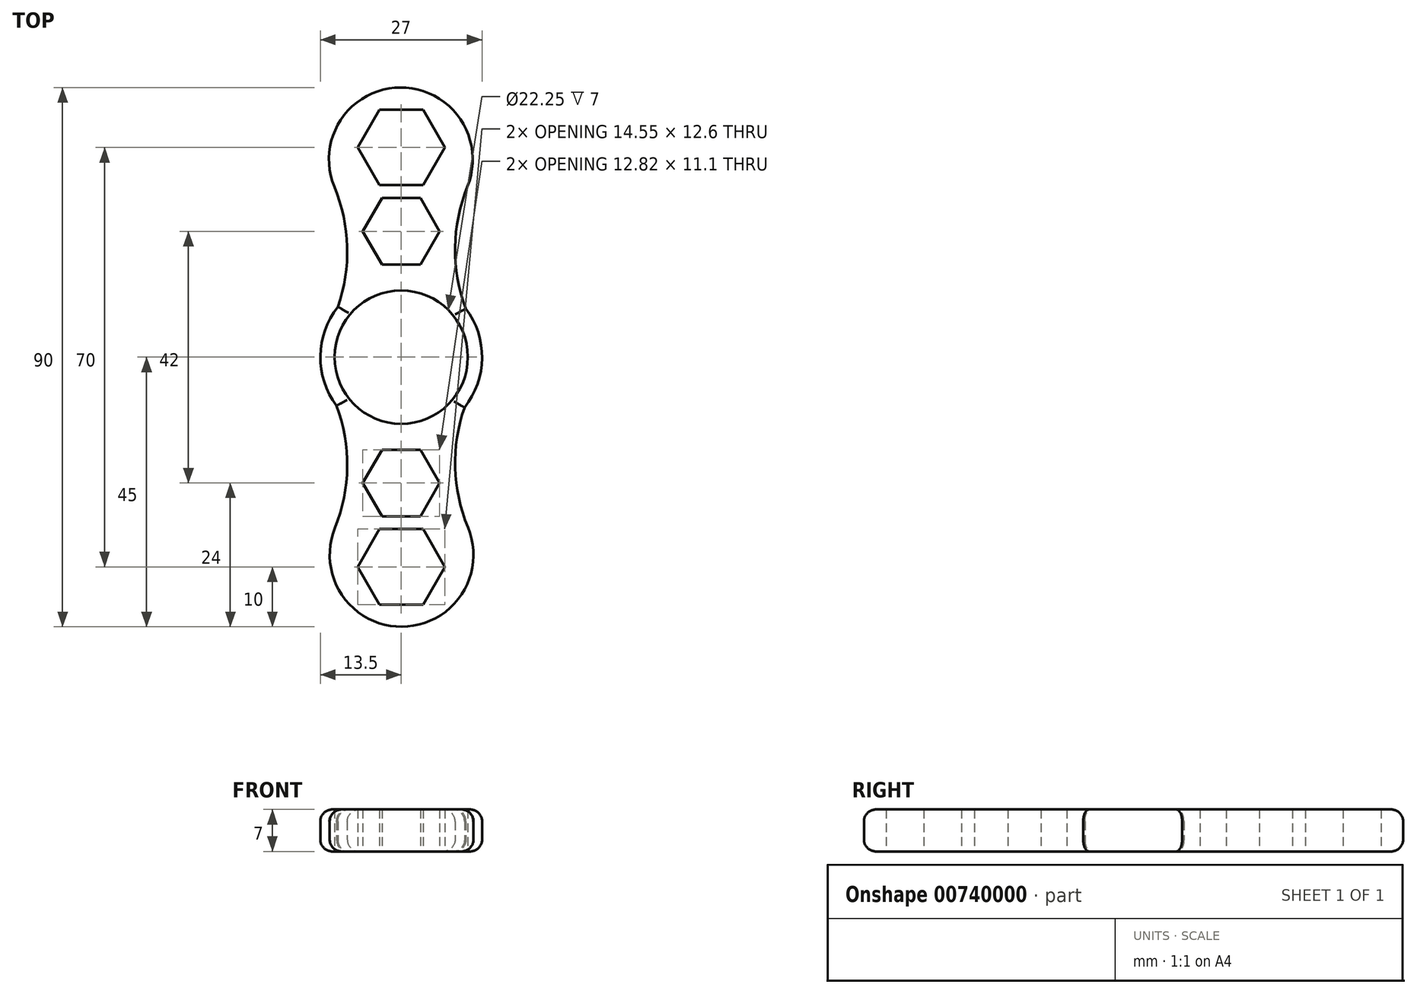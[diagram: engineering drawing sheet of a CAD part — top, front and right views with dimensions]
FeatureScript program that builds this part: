
annotation { "Feature Type Name" : "Feature", "Feature Type Description" : "" }
export const myFeature = defineFeature(function(context is Context, id is Id, definition is map)
    precondition{}
    {
        {
            var Q0;
            Q0=qCreatedBy(makeId("Top.planeOp"),FACE);
            var sketch = newSketch(context, id + "F0", { "sketchPlane" : qUnion([Q0])});
            skCircle(sketch, "E0", {"center": v(0, 0) * mm, "radius": 11.12 * mm});
            skCircle(sketch, "E1.cCircle", {"center": v(0, 21) * mm, "radius": 5.55 * mm, "construction": true});
            skLineSegment(sketch, "E1.0", {"start": v(3.2, 15.45) * mm, "end": v(-3.2, 15.45) * mm});
            skLineSegment(sketch, "E1.1", {"start": v(-3.2, 15.45) * mm, "end": v(-6.4, 21) * mm});
            skLineSegment(sketch, "E1.2", {"start": v(-6.4, 21) * mm, "end": v(-3.2, 26.55) * mm});
            skLineSegment(sketch, "E1.3", {"start": v(-3.2, 26.55) * mm, "end": v(3.2, 26.55) * mm});
            skLineSegment(sketch, "E1.4", {"start": v(3.2, 26.55) * mm, "end": v(6.4, 21) * mm});
            skLineSegment(sketch, "E1.5", {"start": v(6.4, 21) * mm, "end": v(3.2, 15.45) * mm});
            skPoint(sketch, "E1.0.midPoint", {"position": v(0, 15.45) * mm});
            skArc(sketch, "E2", {"start": v(-13.18, 2.92) * mm, "mid": v(0.28, -13.5) * mm, "end": v(13.05, 3.46) * mm});
            skArc(sketch, "E3", {"start": v(-5.62, 22.36) * mm, "mid": v(-5.51, 22.3) * mm, "end": v(-5.4, 22.25) * mm});
            skArc(sketch, "E4", {"start": v(-13.18, 2.92) * mm, "mid": v(-9.09, 15.41) * mm, "end": v(-11.15, 28.4) * mm});
            skArc(sketch, "E5", {"start": v(11.05, 28.49) * mm, "mid": v(9.09, 15.74) * mm, "end": v(13.05, 3.46) * mm});
            skPoint(sketch, "E6", {"position": v(0, 26.55) * mm});
            skCircle(sketch, "E7.cCircle", {"center": v(0, 35) * mm, "radius": 6.3 * mm, "construction": true});
            skLineSegment(sketch, "E7.0", {"start": v(3.64, 28.7) * mm, "end": v(-3.64, 28.7) * mm});
            skLineSegment(sketch, "E7.1", {"start": v(-3.64, 28.7) * mm, "end": v(-7.27, 35) * mm});
            skLineSegment(sketch, "E7.2", {"start": v(-7.27, 35) * mm, "end": v(-3.64, 41.3) * mm});
            skLineSegment(sketch, "E7.3", {"start": v(-3.64, 41.3) * mm, "end": v(3.64, 41.3) * mm});
            skLineSegment(sketch, "E7.4", {"start": v(3.64, 41.3) * mm, "end": v(7.27, 35) * mm});
            skLineSegment(sketch, "E7.5", {"start": v(7.27, 35) * mm, "end": v(3.64, 28.7) * mm});
            skPoint(sketch, "E7.0.midPoint", {"position": v(0, 28.7) * mm});
            skArc(sketch, "E8.trimOffspring", {"start": v(5.4, 22.31) * mm, "mid": v(5.5, 22.37) * mm, "end": v(5.6, 22.42) * mm});
            skArc(sketch, "E9.trimOffspring", {"start": v(11.05, 28.49) * mm, "mid": v(-0.12, 45) * mm, "end": v(-11.15, 28.4) * mm});
            skSolve(sketch);
        }
        {
            var Q0;
            Q0=makeQuery(id+"F0.imprint","IMPRINT",FACE,{"disambiguationData":[TD([[makeQuery(id+"F0.imprint","IMPRINT",EDGE,{"derivedFrom":sQuery(id+"F0.wireOp",EDGE,"E0")}),-1.0]])]});
            extrude(context, id + "F1", {"entities" : qUnion([Q0]), "depth" : 7 * mm, "offsetDistance" : 25 * mm});
        }
        {
            var Q0;
            Q0=makeQuery(id+"F1.opExtrude","SWEPT_BODY",BODY,{"disambiguationData":[OSD([sQuery(id+"F0.wireOp",EDGE,"E0"),sQuery(id+"F0.wireOp",EDGE,"E1.0"),sQuery(id+"F0.wireOp",EDGE,"E1.1"),sQuery(id+"F0.wireOp",EDGE,"E1.2"),sQuery(id+"F0.wireOp",EDGE,"E1.3"),sQuery(id+"F0.wireOp",EDGE,"E1.4"),sQuery(id+"F0.wireOp",EDGE,"E1.5"),sQuery(id+"F0.wireOp",EDGE,"E2"),sQuery(id+"F0.wireOp",EDGE,"E4"),sQuery(id+"F0.wireOp",EDGE,"E5"),sQuery(id+"F0.wireOp",EDGE,"E7.0"),sQuery(id+"F0.wireOp",EDGE,"E7.1"),sQuery(id+"F0.wireOp",EDGE,"E7.2"),sQuery(id+"F0.wireOp",EDGE,"E7.3"),sQuery(id+"F0.wireOp",EDGE,"E7.4"),sQuery(id+"F0.wireOp",EDGE,"E7.5"),sQuery(id+"F0.wireOp",EDGE,"E9.trimOffspring")])]});
            var Q1;
            Q1=makeQuery(id+"F1.opExtrude","CAP_EDGE",EDGE,{"disambiguationData":[OSD([sQuery(id+"F0.wireOp",EDGE,"E0")])],"isStart":false});
            circularPattern(context, id + "F2", {"entities" : qUnion([Q0]), "axis" : qUnion([Q1]), "angle" : 360 * degree, "instanceCount" : 2, "equalSpace" : true});
        }
        {
            var Q0;
            Q0=makeQuery(id+"F2.opPattern","COPY",BODY,{"derivedFrom":makeQuery(id+"F1.opExtrude","SWEPT_BODY",BODY,{"disambiguationData":[OSD([sQuery(id+"F0.wireOp",EDGE,"E0"),sQuery(id+"F0.wireOp",EDGE,"E1.0"),sQuery(id+"F0.wireOp",EDGE,"E1.1"),sQuery(id+"F0.wireOp",EDGE,"E1.2"),sQuery(id+"F0.wireOp",EDGE,"E1.3"),sQuery(id+"F0.wireOp",EDGE,"E1.4"),sQuery(id+"F0.wireOp",EDGE,"E1.5"),sQuery(id+"F0.wireOp",EDGE,"E2"),sQuery(id+"F0.wireOp",EDGE,"E4"),sQuery(id+"F0.wireOp",EDGE,"E5"),sQuery(id+"F0.wireOp",EDGE,"E7.0"),sQuery(id+"F0.wireOp",EDGE,"E7.1"),sQuery(id+"F0.wireOp",EDGE,"E7.2"),sQuery(id+"F0.wireOp",EDGE,"E7.3"),sQuery(id+"F0.wireOp",EDGE,"E7.4"),sQuery(id+"F0.wireOp",EDGE,"E7.5"),sQuery(id+"F0.wireOp",EDGE,"E9.trimOffspring")])]}),"instanceName":"1"});
            var Q1;
            Q1=makeQuery(id+"F1.opExtrude","SWEPT_BODY",BODY,{"disambiguationData":[OSD([sQuery(id+"F0.wireOp",EDGE,"E0"),sQuery(id+"F0.wireOp",EDGE,"E1.0"),sQuery(id+"F0.wireOp",EDGE,"E1.1"),sQuery(id+"F0.wireOp",EDGE,"E1.2"),sQuery(id+"F0.wireOp",EDGE,"E1.3"),sQuery(id+"F0.wireOp",EDGE,"E1.4"),sQuery(id+"F0.wireOp",EDGE,"E1.5"),sQuery(id+"F0.wireOp",EDGE,"E2"),sQuery(id+"F0.wireOp",EDGE,"E4"),sQuery(id+"F0.wireOp",EDGE,"E5"),sQuery(id+"F0.wireOp",EDGE,"E7.0"),sQuery(id+"F0.wireOp",EDGE,"E7.1"),sQuery(id+"F0.wireOp",EDGE,"E7.2"),sQuery(id+"F0.wireOp",EDGE,"E7.3"),sQuery(id+"F0.wireOp",EDGE,"E7.4"),sQuery(id+"F0.wireOp",EDGE,"E7.5"),sQuery(id+"F0.wireOp",EDGE,"E9.trimOffspring")])]});
            booleanBodies(context, id + "F3", {"operationType" : BooleanOperationType.UNION, "tools" : qUnion([Q0, Q1])});
        }
        {
            var Q0;
            Q0=makeQuery(id+"F1.opExtrude","CAP_EDGE",EDGE,{"disambiguationData":[OSD([sQuery(id+"F0.wireOp",EDGE,"E9.trimOffspring")])],"isStart":false});
            var Q1;
            Q1=makeQuery(id+"F1.opExtrude","CAP_EDGE",EDGE,{"disambiguationData":[OSD([sQuery(id+"F0.wireOp",EDGE,"E4")])],"isStart":false});
            var Q2;
            {var subQ0=makeQuery(id+"F1.opExtrude","CAP_EDGE",EDGE,{"disambiguationData":[OSD([sQuery(id+"F0.wireOp",EDGE,"E2")])],"isStart":false});Q2=makeQuery(id+"F3.opBoolean","MERGE",EDGE,{"disambiguationData":[OD(0.0)],"derivedFrom":[subQ0,makeQuery(id+"F2.opPattern","COPY",EDGE,{"derivedFrom":subQ0,"instanceName":"1"})]});}
            var Q3;
            Q3=makeQuery(id+"F2.opPattern","COPY",EDGE,{"derivedFrom":makeQuery(id+"F1.opExtrude","CAP_EDGE",EDGE,{"disambiguationData":[OSD([sQuery(id+"F0.wireOp",EDGE,"E5")])],"isStart":false}),"instanceName":"1"});
            var Q4;
            Q4=makeQuery(id+"F2.opPattern","COPY",EDGE,{"derivedFrom":makeQuery(id+"F1.opExtrude","CAP_EDGE",EDGE,{"disambiguationData":[OSD([sQuery(id+"F0.wireOp",EDGE,"E9.trimOffspring")])],"isStart":false}),"instanceName":"1"});
            var Q5;
            {var subQ0=makeQuery(id+"F1.opExtrude","CAP_EDGE",EDGE,{"disambiguationData":[OSD([sQuery(id+"F0.wireOp",EDGE,"E2")])],"isStart":false});Q5=makeQuery(id+"F3.opBoolean","MERGE",EDGE,{"disambiguationData":[OD(1.0)],"derivedFrom":[subQ0,makeQuery(id+"F2.opPattern","COPY",EDGE,{"derivedFrom":subQ0,"instanceName":"1"})]});}
            var Q6;
            Q6=makeQuery(id+"F1.opExtrude","CAP_EDGE",EDGE,{"disambiguationData":[OSD([sQuery(id+"F0.wireOp",EDGE,"E9.trimOffspring")])],"isStart":true});
            var Q7;
            Q7=makeQuery(id+"F1.opExtrude","CAP_EDGE",EDGE,{"disambiguationData":[OSD([sQuery(id+"F0.wireOp",EDGE,"E5")])],"isStart":true});
            var Q8;
            {var subQ0=makeQuery(id+"F1.opExtrude","CAP_EDGE",EDGE,{"disambiguationData":[OSD([sQuery(id+"F0.wireOp",EDGE,"E2")])],"isStart":true});Q8=makeQuery(id+"F3.opBoolean","MERGE",EDGE,{"disambiguationData":[OD(0.0)],"derivedFrom":[subQ0,makeQuery(id+"F2.opPattern","COPY",EDGE,{"derivedFrom":subQ0,"instanceName":"1"})]});}
            var Q9;
            Q9=makeQuery(id+"F2.opPattern","COPY",EDGE,{"derivedFrom":makeQuery(id+"F1.opExtrude","CAP_EDGE",EDGE,{"disambiguationData":[OSD([sQuery(id+"F0.wireOp",EDGE,"E5")])],"isStart":true}),"instanceName":"1"});
            var Q10;
            Q10=makeQuery(id+"F2.opPattern","COPY",EDGE,{"derivedFrom":makeQuery(id+"F1.opExtrude","CAP_EDGE",EDGE,{"disambiguationData":[OSD([sQuery(id+"F0.wireOp",EDGE,"E9.trimOffspring")])],"isStart":true}),"instanceName":"1"});
            var Q11;
            {var subQ0=makeQuery(id+"F1.opExtrude","CAP_EDGE",EDGE,{"disambiguationData":[OSD([sQuery(id+"F0.wireOp",EDGE,"E2")])],"isStart":true});Q11=makeQuery(id+"F3.opBoolean","MERGE",EDGE,{"disambiguationData":[OD(1.0)],"derivedFrom":[subQ0,makeQuery(id+"F2.opPattern","COPY",EDGE,{"derivedFrom":subQ0,"instanceName":"1"})]});}
            var Q12;
            Q12=makeQuery(id+"F2.opPattern","COPY",EDGE,{"derivedFrom":makeQuery(id+"F1.opExtrude","CAP_EDGE",EDGE,{"disambiguationData":[OSD([sQuery(id+"F0.wireOp",EDGE,"E4")])],"isStart":true}),"instanceName":"1"});
            var Q13;
            Q13=makeQuery(id+"F1.opExtrude","CAP_EDGE",EDGE,{"disambiguationData":[OSD([sQuery(id+"F0.wireOp",EDGE,"E4")])],"isStart":true});
            var Q14;
            Q14=makeQuery(id+"F1.opExtrude","CAP_EDGE",EDGE,{"disambiguationData":[OSD([sQuery(id+"F0.wireOp",EDGE,"E5")])],"isStart":false});
            var Q15;
            Q15=makeQuery(id+"F2.opPattern","COPY",EDGE,{"derivedFrom":makeQuery(id+"F1.opExtrude","CAP_EDGE",EDGE,{"disambiguationData":[OSD([sQuery(id+"F0.wireOp",EDGE,"E4")])],"isStart":false}),"instanceName":"1"});
            fillet(context, id + "F4", {"entities" : qUnion([Q0, Q1, Q2, Q3, Q4, Q5, Q6, Q7, Q8, Q9, Q10, Q11, Q12, Q13, Q14, Q15]), "radius" : 2 * mm, "allowEdgeOverflow" : false});
        }
    });
